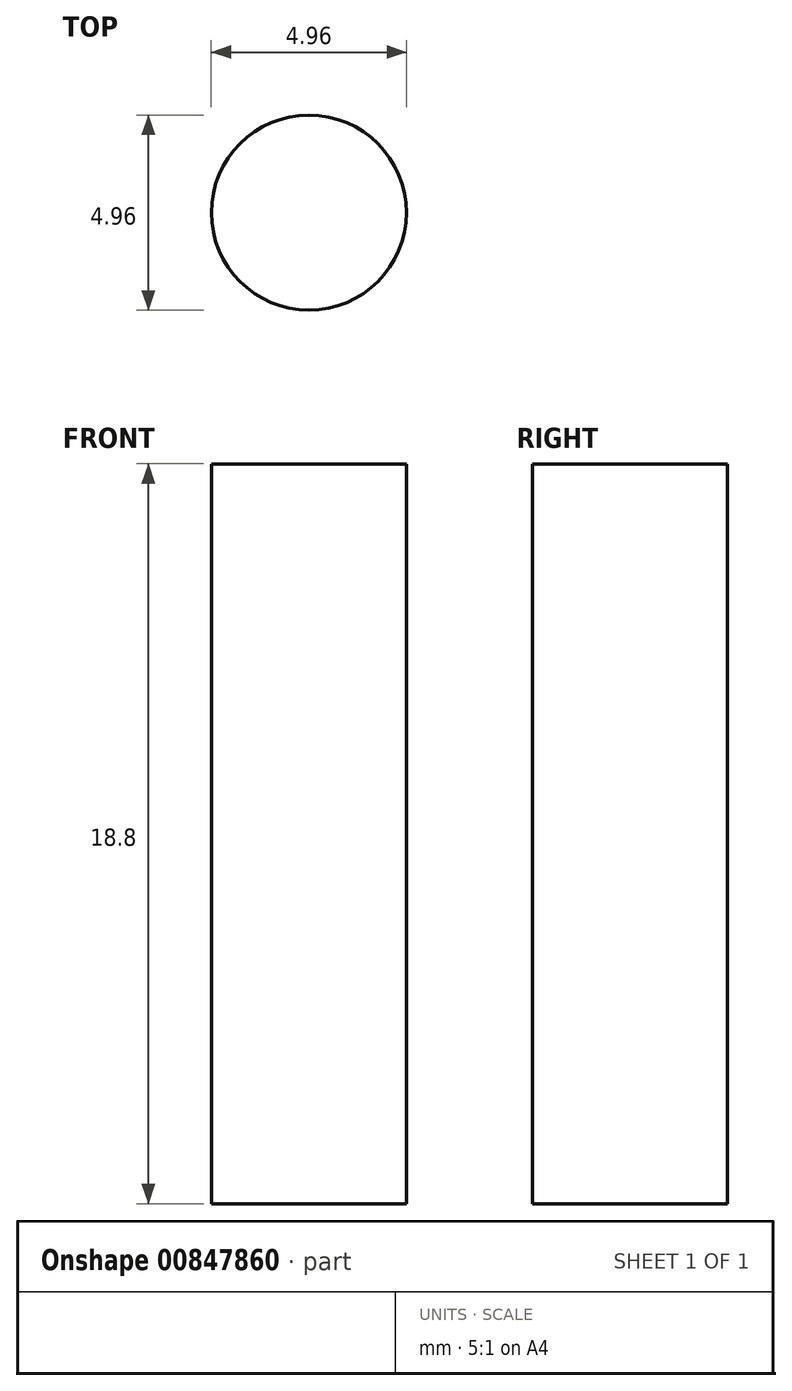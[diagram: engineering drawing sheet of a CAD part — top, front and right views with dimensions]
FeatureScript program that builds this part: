
annotation { "Feature Type Name" : "Feature", "Feature Type Description" : "" }
export const myFeature = defineFeature(function(context is Context, id is Id, definition is map)
    precondition{}
    {
        {
            var Q0;
            Q0=qCreatedBy(makeId("Top.planeOp"),FACE);
            var sketch = newSketch(context, id + "F0", { "sketchPlane" : qUnion([Q0])});
            skCircle(sketch, "E0", {"center": v(0, 0) * mm, "radius": 2.48 * mm});
            skSolve(sketch);
        }
        {
            var Q0;
            Q0=qSketchRegion(id+"F0",true);
            extrude(context, id + "F1", {"entities" : qUnion([Q0]), "depth" : 18.8 * mm, "offsetDistance" : 25.4 * mm});
        }
    });
